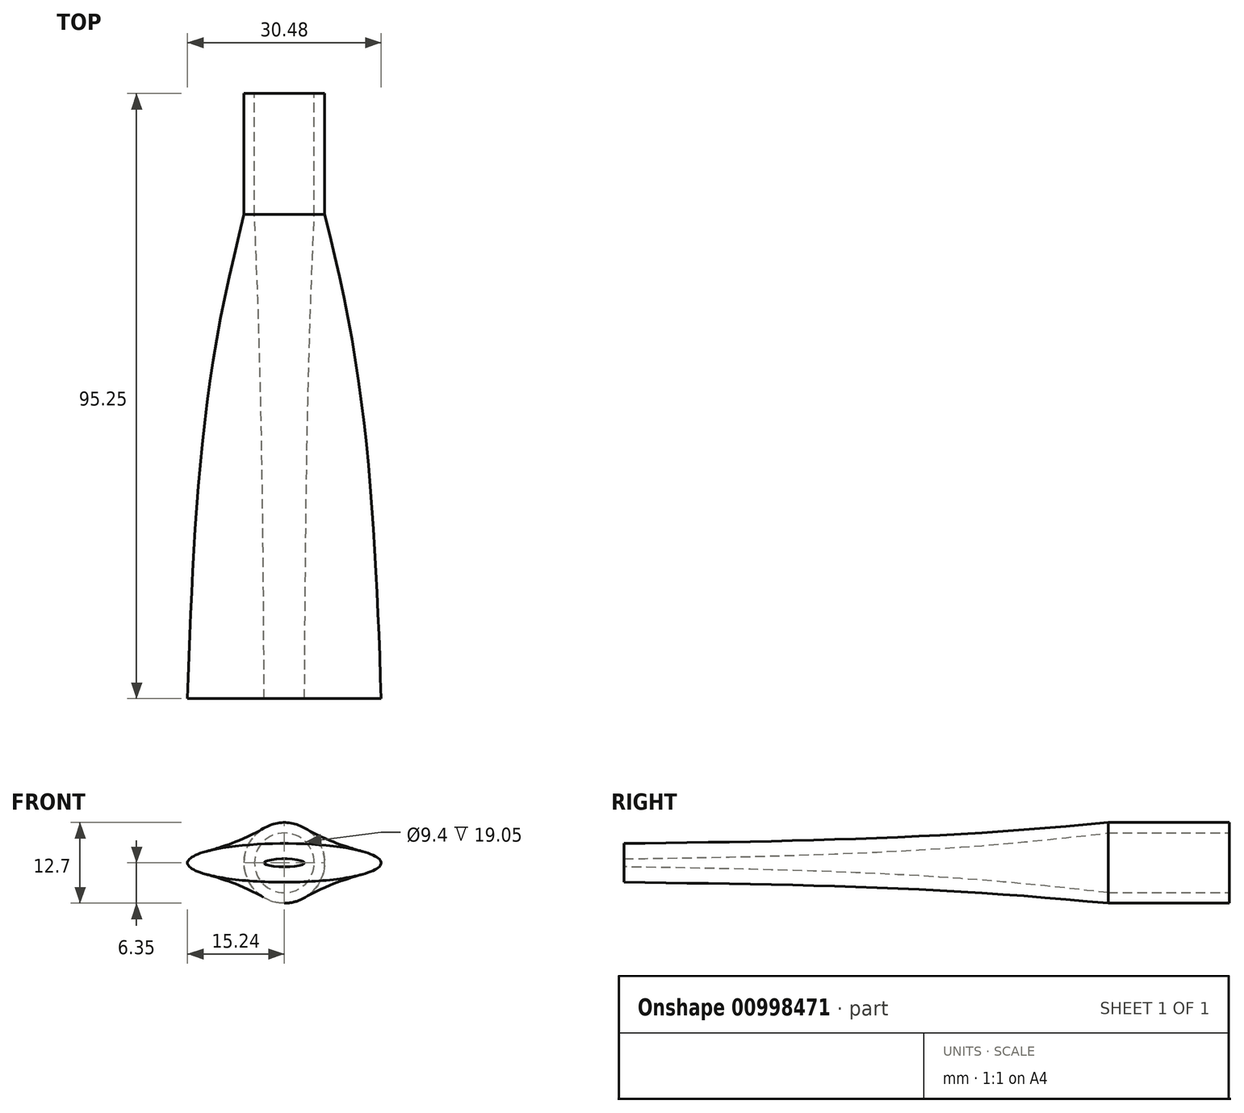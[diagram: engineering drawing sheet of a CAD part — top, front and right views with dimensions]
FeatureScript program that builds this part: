
annotation { "Feature Type Name" : "Feature", "Feature Type Description" : "" }
export const myFeature = defineFeature(function(context is Context, id is Id, definition is map)
    precondition{}
    {
        {
            var Q0;
            Q0=qCreatedBy(makeId("Front.planeOp"),FACE);
            var sketch = newSketch(context, id + "F0", { "sketchPlane" : qUnion([Q0])});
            skCircle(sketch, "E0", {"center": v(0, 0) * mm, "radius": 6.35 * mm});
            skCircle(sketch, "E1", {"center": v(0, 0) * mm, "radius": 4.7 * mm});
            skSolve(sketch);
        }
        {
            var Q0;
            Q0=qSketchRegion(id+"F0",true);
            extrude(context, id + "F1", {"entities" : qUnion([Q0]), "depth" : 19.05 * mm, "offsetDistance" : 25.4 * mm});
        }
        {
            var Q0;
            Q0=makeQuery(id+"F1.opExtrude","CAP_FACE",FACE,{"disambiguationData":[OSD([sQuery(id+"F0.wireOp",EDGE,"E0"),sQuery(id+"F0.wireOp",EDGE,"E1")])],"isStart":false});
            var sketch = newSketch(context, id + "F2", { "sketchPlane" : qUnion([Q0])});
            skCircle(sketch, "E2", {"center": v(0, 0) * mm, "radius": 6.35 * mm});
            skCircle(sketch, "E3", {"center": v(0, 0) * mm, "radius": 4.7 * mm});
            skSolve(sketch);
        }
        {
            var Q0;
            Q0=makeQuery(id+"F2.imprint","IMPRINT",FACE,{"disambiguationData":[TD([[makeQuery(id+"F2.imprint","IMPRINT",EDGE,{"derivedFrom":sQuery(id+"F2.wireOp",EDGE,"E2")}),1.0]])]});
            cPlane(context, id + "F3", {"entities" : qUnion([Q0]), "cplaneType" : CPlaneType.OFFSET, "offset" : 12.7 * mm, "width" : 152.4 * mm, "height" : 152.4 * mm});
        }
        {
            var Q0;
            Q0=makeQuery(id+"F2.imprint","IMPRINT",FACE,{"disambiguationData":[TD([[makeQuery(id+"F2.imprint","IMPRINT",EDGE,{"derivedFrom":sQuery(id+"F2.wireOp",EDGE,"E2")}),1.0]])]});
            var sketch = newSketch(context, id + "F4", { "sketchPlane" : qUnion([Q0])});
            skCircle(sketch, "E4.0.0", {"center": v(0, 0) * mm, "radius": 6.35 * mm});
            skSolve(sketch);
        }
        {
            var Q0;
            Q0=qCreatedBy(id+"F3.planeOp",FACE);
            var sketch = newSketch(context, id + "F5", { "sketchPlane" : qUnion([Q0])});
            skEllipse(sketch, "E5", {"center": v(0, 0) * mm, "majorRadius": 9.31 * mm, "minorRadius": 5.25 * mm, "majorAxis": v(-1, 0)});
            skSolve(sketch);
        }
        {
            var Q0;
            Q0=makeQuery(id+"F4.imprint","IMPRINT",FACE,{"disambiguationData":[TD([[makeQuery(id+"F4.imprint","IMPRINT",EDGE,{"derivedFrom":sQuery(id+"F4.wireOp",EDGE,"E4.0.0")}),1.0]])]});
            cPlane(context, id + "F6", {"entities" : qUnion([Q0]), "cplaneType" : CPlaneType.OFFSET, "offset" : 76.2 * mm, "width" : 152.4 * mm, "height" : 152.4 * mm});
        }
        {
            var Q0;
            Q0=qCreatedBy(id+"F6.planeOp",FACE);
            var sketch = newSketch(context, id + "F7", { "sketchPlane" : qUnion([Q0])});
            skEllipse(sketch, "E6", {"center": v(0, 0) * mm, "majorRadius": 15.24 * mm, "minorRadius": 3.05 * mm, "majorAxis": v(-1, 0)});
            skSolve(sketch);
        }
        {
            var Q1;
            Q1=qSketchRegion(id+"F4",true);
            var Q2;
            Q2=qSketchRegion(id+"F5",true);
            var Q3;
            Q3=qSketchRegion(id+"F7",true);
            loft(context, id + "F8", {"operationType" : NewBodyOperationType.ADD, "sheetProfilesArray" : [{ "sheetProfileEntities" : qUnion([Q1]) }, { "sheetProfileEntities" : qUnion([Q2]) }, { "sheetProfileEntities" : qUnion([Q3]) }]});
        }
        {
            var Q0;
            Q0=qCreatedBy(id+"F6.planeOp",FACE);
            var sketch = newSketch(context, id + "F9", { "sketchPlane" : qUnion([Q0])});
            skEllipse(sketch, "E7", {"center": v(0, 0) * mm, "majorRadius": 3.18 * mm, "minorRadius": 0.64 * mm, "majorAxis": v(-1, 0)});
            skSolve(sketch);
        }
        {
            var Q0;
            Q0=qCreatedBy(id+"F3.planeOp",FACE);
            var sketch = newSketch(context, id + "F10", { "sketchPlane" : qUnion([Q0])});
            skEllipse(sketch, "E8", {"center": v(0, 0) * mm, "majorRadius": 4.2 * mm, "minorRadius": 3.34 * mm, "majorAxis": v(-1, 0)});
            skSolve(sketch);
        }
        {
            var Q0;
            Q0=qCreatedBy(id+"F3.planeOp",FACE);
            cPlane(context, id + "F11", {"entities" : qUnion([Q0]), "cplaneType" : CPlaneType.OFFSET, "offset" : 12.7 * mm, "oppositeDirection" : true, "width" : 152.4 * mm, "height" : 152.4 * mm});
        }
        {
            var Q0;
            Q0=qCreatedBy(id+"F11.planeOp",FACE);
            var sketch = newSketch(context, id + "F12", { "sketchPlane" : qUnion([Q0])});
            skCircle(sketch, "E9", {"center": v(0, 0) * mm, "radius": 4.7 * mm});
            skSolve(sketch);
        }
        {
            var Q1;
            Q1=qSketchRegion(id+"F12",true);
            var Q2;
            Q2=qSketchRegion(id+"F10",true);
            var Q3;
            Q3=qSketchRegion(id+"F9",true);
            loft(context, id + "F13", {"operationType" : NewBodyOperationType.REMOVE, "sheetProfilesArray" : [{ "sheetProfileEntities" : qUnion([Q1]) }, { "sheetProfileEntities" : qUnion([Q2]) }, { "sheetProfileEntities" : qUnion([Q3]) }]});
        }
    });
